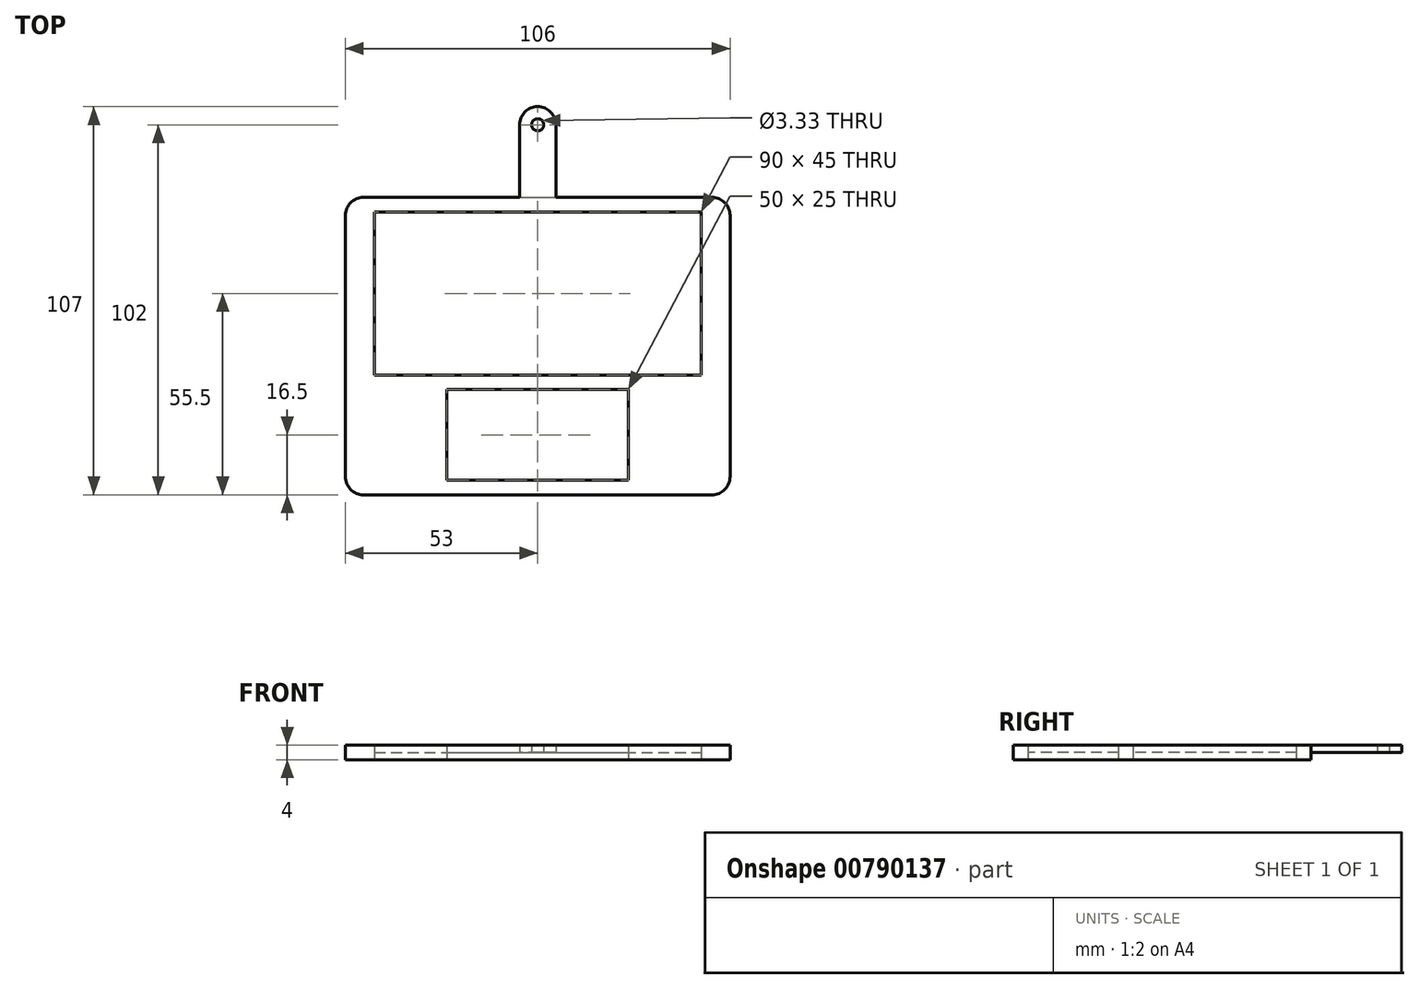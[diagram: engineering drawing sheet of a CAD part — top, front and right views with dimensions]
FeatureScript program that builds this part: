
annotation { "Feature Type Name" : "Feature", "Feature Type Description" : "" }
export const myFeature = defineFeature(function(context is Context, id is Id, definition is map)
    precondition{}
    {
        {
            var Q0;
            Q0=qCreatedBy(makeId("Top.planeOp"),FACE);
            var sketch = newSketch(context, id + "F0", { "sketchPlane" : qUnion([Q0])});
            skLineSegment(sketch, "E0.top", {"start": v(53, -84.5) * mm, "end": v(-53, -84.5) * mm});
            skLineSegment(sketch, "E0.left", {"start": v(53, -2.5) * mm, "end": v(53, -84.5) * mm});
            skLineSegment(sketch, "E0.right", {"start": v(-53, -2.5) * mm, "end": v(-53, -84.5) * mm});
            skPoint(sketch, "E0.middle", {"position": v(0, 0) * mm});
            skPoint(sketch, "E1.orphan", {"position": v(-53, 84.5) * mm});
            skPoint(sketch, "E2.orphan", {"position": v(53, 84.5) * mm});
            skLineSegment(sketch, "E3", {"start": v(-53, -2.5) * mm, "end": v(53, -2.5) * mm});
            skLineSegment(sketch, "E4.left", {"start": v(5, -2.5) * mm, "end": v(5, 17.5) * mm});
            skLineSegment(sketch, "E4.right", {"start": v(-5, -2.5) * mm, "end": v(-5, 17.5) * mm});
            skPoint(sketch, "E5.orphan", {"position": v(-53, 7.5) * mm});
            skCircle(sketch, "E6", {"center": v(0, 17.5) * mm, "radius": 1.67 * mm});
            skLineSegment(sketch, "E7", {"start": v(-45, -6.5) * mm, "end": v(-45, -51.5) * mm});
            skLineSegment(sketch, "E8", {"start": v(45, -6.5) * mm, "end": v(45, -51.5) * mm});
            skLineSegment(sketch, "E9", {"start": v(-45, -51.5) * mm, "end": v(45, -51.5) * mm});
            skLineSegment(sketch, "E10", {"start": v(-45, -6.5) * mm, "end": v(45, -6.5) * mm});
            skLineSegment(sketch, "E11", {"start": v(-25, -55.5) * mm, "end": v(25, -55.5) * mm});
            skLineSegment(sketch, "E12", {"start": v(-25, -55.5) * mm, "end": v(-25, -80.5) * mm});
            skLineSegment(sketch, "E13", {"start": v(-25, -80.5) * mm, "end": v(25, -80.5) * mm});
            skLineSegment(sketch, "E14", {"start": v(25, -80.5) * mm, "end": v(25, -55.5) * mm});
            skLineSegment(sketch, "E15", {"start": v(25, -55.5) * mm, "end": v(-25, -55.5) * mm});
            skPoint(sketch, "E16.end.orphan", {"position": v(15.62, 57.1) * mm});
            skPoint(sketch, "E17.orphan", {"position": v(24, 46) * mm});
            skPoint(sketch, "E18.start.orphan", {"position": v(-24, 46) * mm});
            skPoint(sketch, "E19.start.orphan", {"position": v(-18.78, 34.9) * mm});
            skPoint(sketch, "E20.orphan", {"position": v(-45, -2.5) * mm});
            skPoint(sketch, "E21.orphan", {"position": v(45, -2.5) * mm});
            skPoint(sketch, "E22.start.orphan", {"position": v(-18.78, 77.6) * mm});
            skPoint(sketch, "E23.orphan", {"position": v(24, 57.1) * mm});
            skPoint(sketch, "E24", {"position": v(0, 101.9) * mm});
            skPoint(sketch, "E25.end.orphan", {"position": v(50.45, 84.5) * mm});
            skPoint(sketch, "E26.trimOffspring.start.orphan", {"position": v(26.9, 84.5) * mm});
            skPoint(sketch, "E27.end.orphan", {"position": v(0.05, 10.43) * mm});
            skPoint(sketch, "E27.start.orphan", {"position": v(-23.5, 12.91) * mm});
            skPoint(sketch, "E28.orphan", {"position": v(23.5, 57.1) * mm});
            skPoint(sketch, "E29.orphan", {"position": v(24, 7.5) * mm});
            skPoint(sketch, "E30.orphan", {"position": v(-24, 7.5) * mm});
            skPoint(sketch, "E31.end.orphan", {"position": v(-23.5, 32.3) * mm});
            skPoint(sketch, "E31.start.orphan", {"position": v(-23.5, 14.75) * mm});
            skPoint(sketch, "E32.start.orphan", {"position": v(-23.5, 34.8) * mm});
            skPoint(sketch, "E33.right.start.orphan", {"position": v(24, 84.5) * mm});
            skPoint(sketch, "E34.end.orphan", {"position": v(23.5, 59.6) * mm});
            skPoint(sketch, "E34.start.orphan", {"position": v(23.5, 77.5) * mm});
            skPoint(sketch, "E33.bottom.start.orphan", {"position": v(-24, 84.5) * mm});
            skPoint(sketch, "E35.end.orphan", {"position": v(5, 17.5) * mm});
            skPoint(sketch, "E35.start.orphan", {"position": v(-5, 17.5) * mm});
            skPoint(sketch, "E36.orphan", {"position": v(5, 16.5) * mm});
            skPoint(sketch, "E37.orphan", {"position": v(-5, 37.5) * mm});
            skArc(sketch, "E38", {"start": v(-5, 17.5) * mm, "mid": v(0, 22.5) * mm, "end": v(5, 17.5) * mm});
            skSolve(sketch);
        }
        {
            var Q0;
            Q0=makeQuery(id+"F0.imprint","IMPRINT",FACE,{"disambiguationData":[TD([[makeQuery(id+"F0.imprint","IMPRINT",EDGE,{"derivedFrom":sQuery(id+"F0.wireOp",EDGE,"E0.top")}),-1.0]])]});
            var Q1;
            Q1=makeQuery(id+"F0.imprint","IMPRINT",FACE,{"disambiguationData":[TD([[makeQuery(id+"F0.imprint","IMPRINT",EDGE,{"derivedFrom":sQuery(id+"F0.wireOp",EDGE,"E4.bottom")}),-1.0]])]});
            extrude(context, id + "F1", {"entities" : qUnion([Q0, Q1]), "depth" : 4 * mm});
        }
        {
            var Q0;
            Q0=makeQuery(id+"F0.imprint","IMPRINT",FACE,{"disambiguationData":[TD([[makeQuery(id+"F0.imprint","IMPRINT",EDGE,{"derivedFrom":sQuery(id+"F0.wireOp",EDGE,"E12")}),1.0]])]});
            var Q1;
            Q1=makeQuery(id+"F0.imprint","IMPRINT",FACE,{"disambiguationData":[TD([[makeQuery(id+"F0.imprint","IMPRINT",EDGE,{"derivedFrom":sQuery(id+"F0.wireOp",EDGE,"E7")}),1.0]])]});
            extrude(context, id + "F2", {"entities" : qUnion([Q0, Q1]), "depth" : 2 * mm});
        }
        {
            var Q0;
            Q0=qCreatedBy(makeId("Top.planeOp"),FACE);
            cPlane(context, id + "F3", {"entities" : qUnion([Q0]), "cplaneType" : CPlaneType.OFFSET, "offset" : 2 * mm, "width" : 150 * mm, "height" : 150 * mm});
        }
        {
            var Q0;
            Q0=qCreatedBy(id+"F3.planeOp",FACE);
            var sketch = newSketch(context, id + "F4", { "sketchPlane" : qUnion([Q0])});
            skLineSegment(sketch, "E39", {"start": v(-4.18, 13.18) * mm, "end": v(-4.18, 18.18) * mm});
            skLineSegment(sketch, "E40", {"start": v(5.82, 13.18) * mm, "end": v(5.82, 18.18) * mm});
            skArc(sketch, "E41", {"start": v(-4.18, 13.18) * mm, "mid": v(0.82, 9.01) * mm, "end": v(5.82, 13.18) * mm});
            skLineSegment(sketch, "E42", {"start": v(-4.18, 18.18) * mm, "end": v(5.82, 18.18) * mm});
            skLineSegment(sketch, "E43", {"start": v(5, 17.5) * mm, "end": v(5, -2.5) * mm});
            skLineSegment(sketch, "E44", {"start": v(5, -2.5) * mm, "end": v(-5, -2.5) * mm});
            skLineSegment(sketch, "E45", {"start": v(-5, -2.5) * mm, "end": v(-16.41, 4.6) * mm});
            skArc(sketch, "E46", {"start": v(5, 17.5) * mm, "mid": v(-8.61, 15.87) * mm, "end": v(-16.41, 4.6) * mm});
            skSolve(sketch);
        }
        {
            var Q0;
            Q0=makeQuery(id+"F4.imprint","IMPRINT",FACE,{"disambiguationData":[TD([[makeQuery(id+"F4.imprint","IMPRINT",EDGE,{"derivedFrom":sQuery(id+"F4.wireOp",EDGE,"E43")}),-1.0]])]});
            extrude(context, id + "F5", {"entities" : qUnion([Q0]), "operationType" : NewBodyOperationType.REMOVE, "endBound" : BoundingType.THROUGH_ALL, "oppositeDirection" : true, "depth" : 25 * mm});
        }
        {
            var Q0;
            Q0=qCreatedBy(makeId("Top.planeOp"),FACE);
            cPlane(context, id + "F6", {"entities" : qUnion([Q0]), "cplaneType" : CPlaneType.OFFSET, "offset" : 4 * mm, "width" : 150 * mm, "height" : 150 * mm});
        }
        {
            var Q0;
            Q0=makeQuery(id+"F1.opExtrude","SWEPT_EDGE",EDGE,{"disambiguationData":[OSD([sQuery(id+"F0.wireOp",EDGE,"E0.top"),sQuery(id+"F0.wireOp",EDGE,"E0.left")])]});
            var Q1;
            Q1=makeQuery(id+"F1.opExtrude","SWEPT_EDGE",EDGE,{"disambiguationData":[OSD([sQuery(id+"F0.wireOp",EDGE,"E0.top"),sQuery(id+"F0.wireOp",EDGE,"E0.right")])]});
            var Q2;
            Q2=makeQuery(id+"F1.opExtrude","SWEPT_EDGE",EDGE,{"disambiguationData":[OSD([sQuery(id+"F0.wireOp",EDGE,"E0.right"),sQuery(id+"F0.wireOp",EDGE,"E3")])]});
            var Q3;
            Q3=makeQuery(id+"F1.opExtrude","SWEPT_EDGE",EDGE,{"disambiguationData":[OSD([sQuery(id+"F0.wireOp",EDGE,"E0.left"),sQuery(id+"F0.wireOp",EDGE,"E3")])]});
            var Q4;
            Q4=makeQuery(id+"F1.opExtrude","SWEPT_EDGE",EDGE,{"disambiguationData":[OSD([sQuery(id+"FFKYT1JyJelcZBP_0.wireOp",EDGE,"fc6cac5f-266f-4da8-866d-79a4c6e8a072.top"),sQuery(id+"FFKYT1JyJelcZBP_0.wireOp",EDGE,"fc6cac5f-266f-4da8-866d-79a4c6e8a072.left")])]});
            var Q5;
            Q5=makeQuery(id+"F1.opExtrude","SWEPT_EDGE",EDGE,{"disambiguationData":[OSD([sQuery(id+"FFKYT1JyJelcZBP_0.wireOp",EDGE,"fc6cac5f-266f-4da8-866d-79a4c6e8a072.top"),sQuery(id+"FFKYT1JyJelcZBP_0.wireOp",EDGE,"fc6cac5f-266f-4da8-866d-79a4c6e8a072.right")])]});
            fillet(context, id + "F7", {"entities" : qUnion([Q0, Q1, Q2, Q3, Q4, Q5]), "radius" : 5 * mm, "tangentPropagation" : true, "allowEdgeOverflow" : false});
        }
        {
            var Q0;
            {var subQ1=sQuery(id+"F0.wireOp",EDGE,"E4.left");Q0=makeQuery(id+"F0.imprint","IMPRINT",FACE,{"disambiguationData":[TD([[makeQuery(id+"F0.imprint","IMPRINT",EDGE,{"derivedFrom":subQ1}),1.0]])]});}
            extrude(context, id + "F8", {"entities" : qUnion([Q0]), "operationType" : NewBodyOperationType.ADD, "depth" : 4 * mm, "offsetDistance" : 25 * mm});
        }
        {
            var Q0;
            {var subQ1=sQuery(id+"F0.wireOp",EDGE,"E4.left");Q0=makeQuery(id+"F0.imprint","IMPRINT",FACE,{"disambiguationData":[TD([[makeQuery(id+"F0.imprint","IMPRINT",EDGE,{"derivedFrom":subQ1}),1.0]])]});}
            extrude(context, id + "F9", {"entities" : qUnion([Q0]), "operationType" : NewBodyOperationType.REMOVE, "depth" : 2 * mm, "offsetDistance" : 25 * mm});
        }
    });
